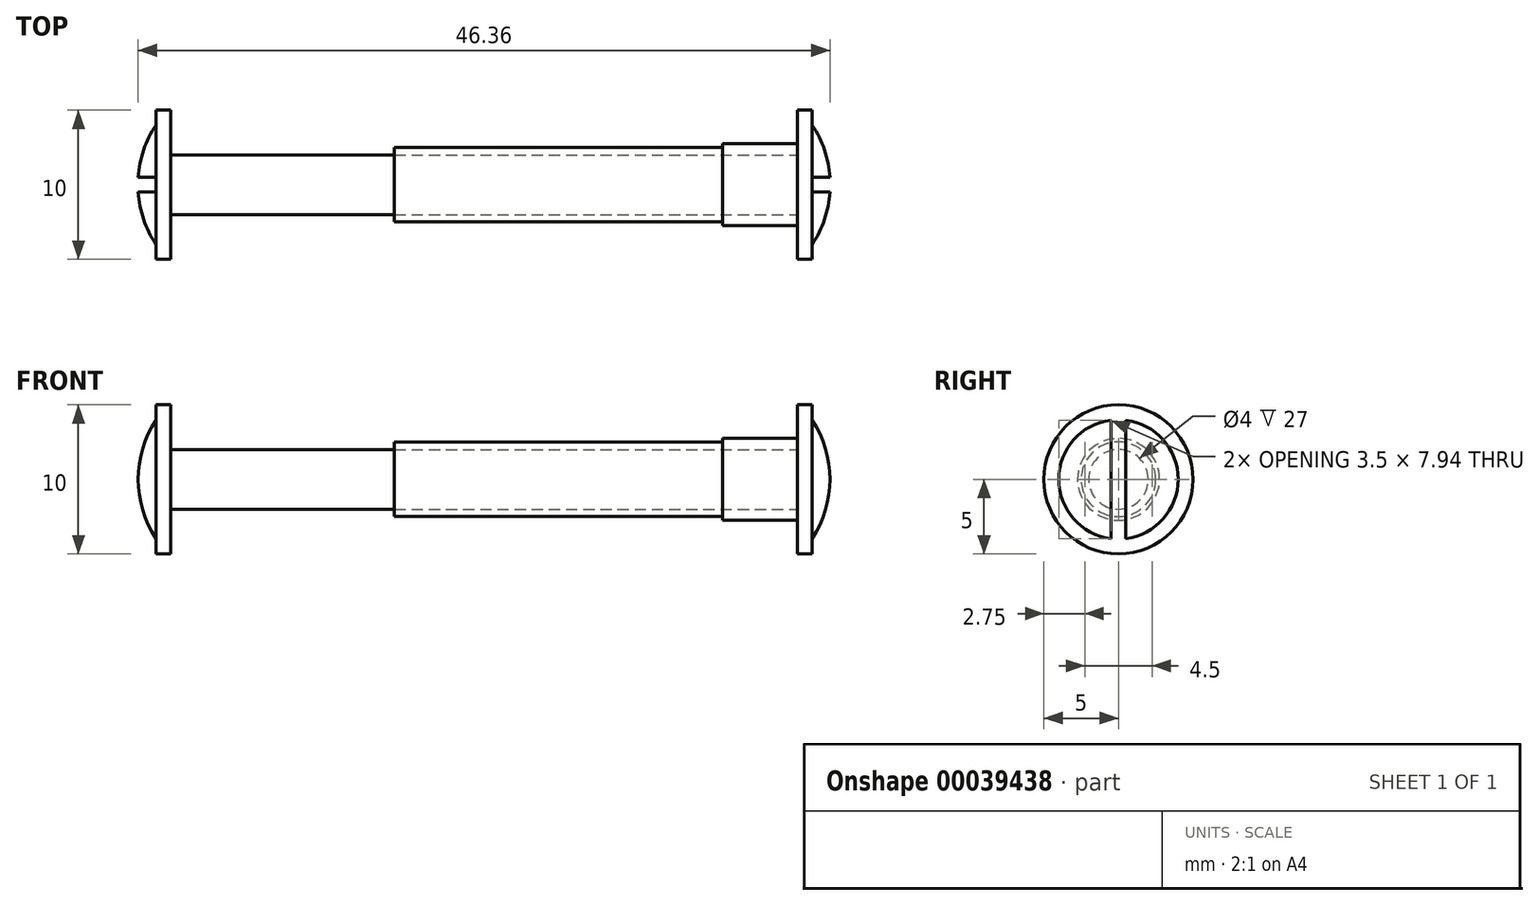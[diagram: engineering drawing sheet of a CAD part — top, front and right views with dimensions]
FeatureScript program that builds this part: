
annotation { "Feature Type Name" : "Feature", "Feature Type Description" : "" }
export const myFeature = defineFeature(function(context is Context, id is Id, definition is map)
    precondition{}
    {
        {
            var Q0;
            Q0=qCreatedBy(makeId("Front.planeOp"),FACE);
            var sketch = newSketch(context, id + "F0", { "sketchPlane" : qUnion([Q0])});
            skLineSegment(sketch, "E0.bottom", {"start": v(0, 0) * mm, "end": v(-15, 0) * mm});
            skLineSegment(sketch, "E0.top", {"start": v(0, 2) * mm, "end": v(-15, 2) * mm});
            skLineSegment(sketch, "E0.left", {"start": v(0, 0) * mm, "end": v(0, 2) * mm});
            skLineSegment(sketch, "E1.bottom", {"start": v(-15, 0) * mm, "end": v(-16, 0) * mm});
            skLineSegment(sketch, "E1.top", {"start": v(-15, 5) * mm, "end": v(-16, 5) * mm});
            skLineSegment(sketch, "E1.left", {"start": v(-15, 2) * mm, "end": v(-15, 5) * mm});
            skLineSegment(sketch, "E1.right", {"start": v(-16, 4) * mm, "end": v(-16, 5) * mm});
            skArc(sketch, "E2", {"start": v(-16, 4) * mm, "mid": v(-16.9, 2.09) * mm, "end": v(-17.2, 0) * mm});
            skLineSegment(sketch, "E3", {"start": v(-16, 0) * mm, "end": v(-17.2, 0) * mm});
            skLineSegment(sketch, "E4", {"start": v(-15, 0) * mm, "end": v(-15, 2) * mm, "construction": true});
            skLineSegment(sketch, "E5", {"start": v(-16, 0) * mm, "end": v(-16, 4) * mm, "construction": true});
            skLineSegment(sketch, "E6.bottom", {"start": v(0, 2) * mm, "end": v(22, 2) * mm});
            skLineSegment(sketch, "E6.top", {"start": v(0, 2.5) * mm, "end": v(22, 2.5) * mm});
            skLineSegment(sketch, "E6.left", {"start": v(0, 2) * mm, "end": v(0, 2.5) * mm});
            skLineSegment(sketch, "E7.bottom", {"start": v(22, 2) * mm, "end": v(27, 2) * mm});
            skLineSegment(sketch, "E7.top", {"start": v(22, 2.75) * mm, "end": v(27, 2.75) * mm});
            skLineSegment(sketch, "E7.left", {"start": v(22, 2) * mm, "end": v(22, 2.75) * mm});
            skLineSegment(sketch, "E7.right", {"start": v(27, 2) * mm, "end": v(27, 2.75) * mm});
            skLineSegment(sketch, "E8.bottom", {"start": v(27, 0) * mm, "end": v(28, 0) * mm});
            skLineSegment(sketch, "E8.top", {"start": v(27, 5) * mm, "end": v(28, 5) * mm});
            skLineSegment(sketch, "E8.left", {"start": v(27, 0) * mm, "end": v(27, 5) * mm});
            skLineSegment(sketch, "E8.right", {"start": v(28, 0) * mm, "end": v(28, 5) * mm});
            skArc(sketch, "E9", {"start": v(29.2, 0) * mm, "mid": v(28.9, 2.09) * mm, "end": v(28, 4) * mm});
            skLineSegment(sketch, "E10", {"start": v(28, 0) * mm, "end": v(29.2, 0) * mm});
            skSolve(sketch);
        }
        {
            var Q0;
            Q0=makeQuery(id+"F0.imprint","IMPRINT",FACE,{"disambiguationData":[TD([[makeQuery(id+"F0.imprint","IMPRINT",EDGE,{"derivedFrom":sQuery(id+"F0.wireOp",EDGE,"E0.bottom")}),-1.0]])]});
            var Q1;
            Q1=sQuery(id+"F0.wireOp",EDGE,"E0.bottom");
            revolve(context, id + "F1", {"entities" : qUnion([Q0]), "axis" : qUnion([Q1]), "revolveType" : RevolveType.FULL});
        }
        {
            var Q0;
            Q0=makeQuery(id+"F1.opRevolve","SWEPT_FACE",FACE,{"disambiguationData":[OSD([sQuery(id+"F0.wireOp",EDGE,"E1.right")])]});
            var sketch = newSketch(context, id + "F2", { "sketchPlane" : qUnion([Q0])});
            skLineSegment(sketch, "E11", {"start": v(0, -4) * mm, "end": v(0, 4) * mm, "construction": true});
            skLineSegment(sketch, "E12", {"start": v(-0.5, 3.97) * mm, "end": v(-0.5, -3.97) * mm});
            skArc(sketch, "E13.0", {"start": v(-0.5, 3.97) * mm, "mid": v(0, 4) * mm, "end": v(0.5, 3.97) * mm});
            skLineSegment(sketch, "E14.MirrorCS", {"start": v(0.5, 3.97) * mm, "end": v(0.5, -3.97) * mm});
            skArc(sketch, "E15.trimOffspring", {"start": v(0.5, -3.97) * mm, "mid": v(0, -4) * mm, "end": v(-0.5, -3.97) * mm});
            skSolve(sketch);
        }
        {
            var Q0;
            Q0 = qSketchRegion(id + "F2", true);
            extrude(context, id + "F3", {"entities" : qUnion([Q0]), "operationType" : NewBodyOperationType.REMOVE, "endBound" : BoundingType.UP_TO_NEXT, "depth" : 25 * mm});
        }
        {
            var Q0;
            {var subQ2=sQuery(id+"F0.wireOp",EDGE,"E6.bottom");Q0=makeQuery(id+"F0.imprint","IMPRINT",FACE,{"disambiguationData":[TD([[makeQuery(id+"F0.imprint","IMPRINT",EDGE,{"derivedFrom":subQ2}),1.0]])]});}
            var Q1;
            {var subQ2=sQuery(id+"F0.wireOp",EDGE,"E7.bottom");Q1=makeQuery(id+"F0.imprint","IMPRINT",FACE,{"disambiguationData":[TD([[makeQuery(id+"F0.imprint","IMPRINT",EDGE,{"derivedFrom":subQ2}),1.0]])]});}
            var Q2;
            {var subQ3=sQuery(id+"F0.wireOp",EDGE,"E8.bottom");Q2=makeQuery(id+"F0.imprint","IMPRINT",FACE,{"disambiguationData":[TD([[makeQuery(id+"F0.imprint","IMPRINT",EDGE,{"derivedFrom":subQ3}),1.0]])]});}
            var Q3;
            {var subQ1=sQuery(id+"F0.wireOp",EDGE,"E9");Q3=makeQuery(id+"F0.imprint","IMPRINT",FACE,{"disambiguationData":[TD([[makeQuery(id+"F0.imprint","IMPRINT",EDGE,{"derivedFrom":subQ1}),1.0]])]});}
            var Q4;
            Q4=sQuery(id+"F0.wireOp",EDGE,"E0.bottom");
            revolve(context, id + "F4", {"entities" : qUnion([Q0, Q1, Q2, Q3]), "axis" : qUnion([Q4]), "revolveType" : RevolveType.FULL});
        }
        {
            var Q0;
            Q0=makeQuery(id+"F4.opRevolve","SWEPT_FACE",FACE,{"disambiguationData":[OSD([sQuery(id+"F0.wireOp",EDGE,"E8.right")])]});
            var sketch = newSketch(context, id + "F5", { "sketchPlane" : qUnion([Q0])});
            skArc(sketch, "E16.0", {"start": v(-0.5, -3.97) * mm, "mid": v(0, -4) * mm, "end": v(0.5, -3.97) * mm});
            skLineSegment(sketch, "E17", {"start": v(0, 4) * mm, "end": v(0, -4) * mm, "construction": true});
            skLineSegment(sketch, "E18", {"start": v(-0.5, 3.97) * mm, "end": v(-0.5, -3.97) * mm});
            skLineSegment(sketch, "E19.MirrorCS", {"start": v(0.5, 3.97) * mm, "end": v(0.5, -3.97) * mm});
            skArc(sketch, "E20.trimOffspring", {"start": v(0.5, 3.97) * mm, "mid": v(0, 4) * mm, "end": v(-0.5, 3.97) * mm});
            skSolve(sketch);
        }
        {
            var Q0;
            Q0 = qSketchRegion(id + "F5", true);
            extrude(context, id + "F6", {"entities" : qUnion([Q0]), "operationType" : NewBodyOperationType.REMOVE, "endBound" : BoundingType.UP_TO_NEXT, "depth" : 25 * mm});
        }
    });
